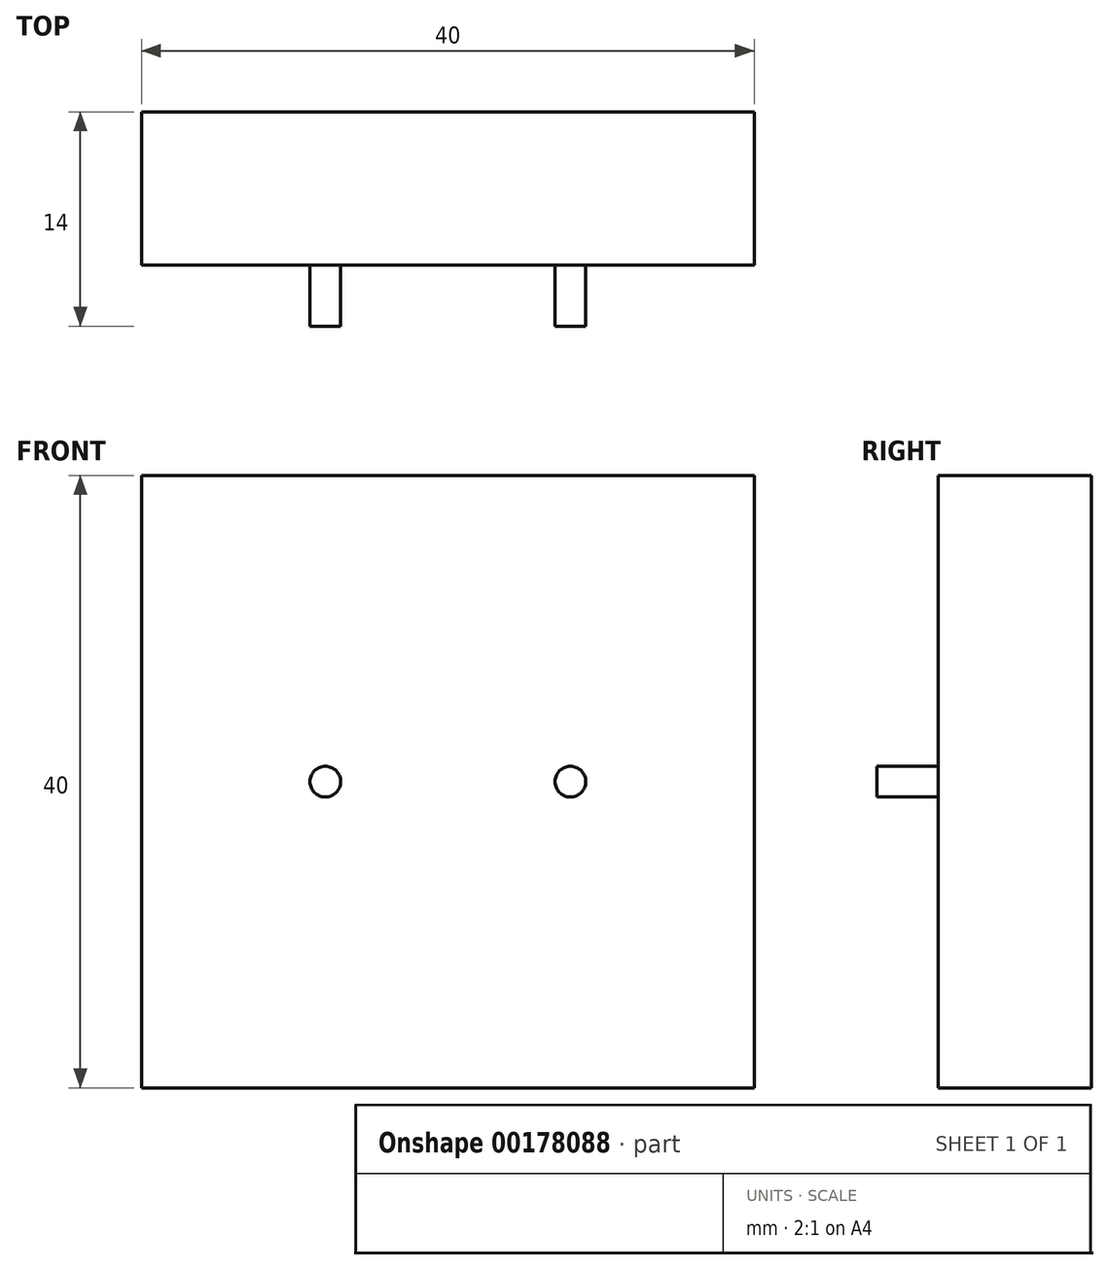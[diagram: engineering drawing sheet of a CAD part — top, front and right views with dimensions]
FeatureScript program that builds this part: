
annotation { "Feature Type Name" : "Feature", "Feature Type Description" : "" }
export const myFeature = defineFeature(function(context is Context, id is Id, definition is map)
    precondition{}
    {
        {
            var Q0;
            Q0=qCreatedBy(makeId("Right.planeOp"),FACE);
            var sketch = newSketch(context, id + "F0", { "sketchPlane" : qUnion([Q0])});
            skLineSegment(sketch, "E0.bottom", {"start": v(5, 20) * mm, "end": v(-5, 20) * mm});
            skLineSegment(sketch, "E0.top", {"start": v(5, -20) * mm, "end": v(-5, -20) * mm});
            skLineSegment(sketch, "E0.left", {"start": v(5, 20) * mm, "end": v(5, -20) * mm});
            skLineSegment(sketch, "E0.right", {"start": v(-5, 20) * mm, "end": v(-5, -20) * mm});
            skPoint(sketch, "E0.middle", {"position": v(0, 0) * mm});
            skSolve(sketch);
        }
        {
            var Q0;
            Q0 = qSketchRegion(id + "F0", true);
            extrude(context, id + "F1", {"entities" : qUnion([Q0]), "depth" : 20 * mm, "hasSecondDirection" : true, "secondDirectionOppositeDirection" : true, "secondDirectionDepth" : 20 * mm});
        }
        {
            var Q0;
            Q0=makeQuery(id+"F1.opExtrude","SWEPT_FACE",FACE,{"disambiguationData":[OSD([sQuery(id+"F0.wireOp",EDGE,"E0.right")])]});
            var sketch = newSketch(context, id + "F2", { "sketchPlane" : qUnion([Q0])});
            skCircle(sketch, "E1", {"center": v(-8, 0) * mm, "radius": 1 * mm});
            skCircle(sketch, "E2", {"center": v(8, 0) * mm, "radius": 1 * mm});
            skSolve(sketch);
        }
        {
            var Q0;
            Q0 = qSketchRegion(id + "F2", true);
            extrude(context, id + "F3", {"entities" : qUnion([Q0]), "operationType" : NewBodyOperationType.ADD, "depth" : 4 * mm});
        }
    });
